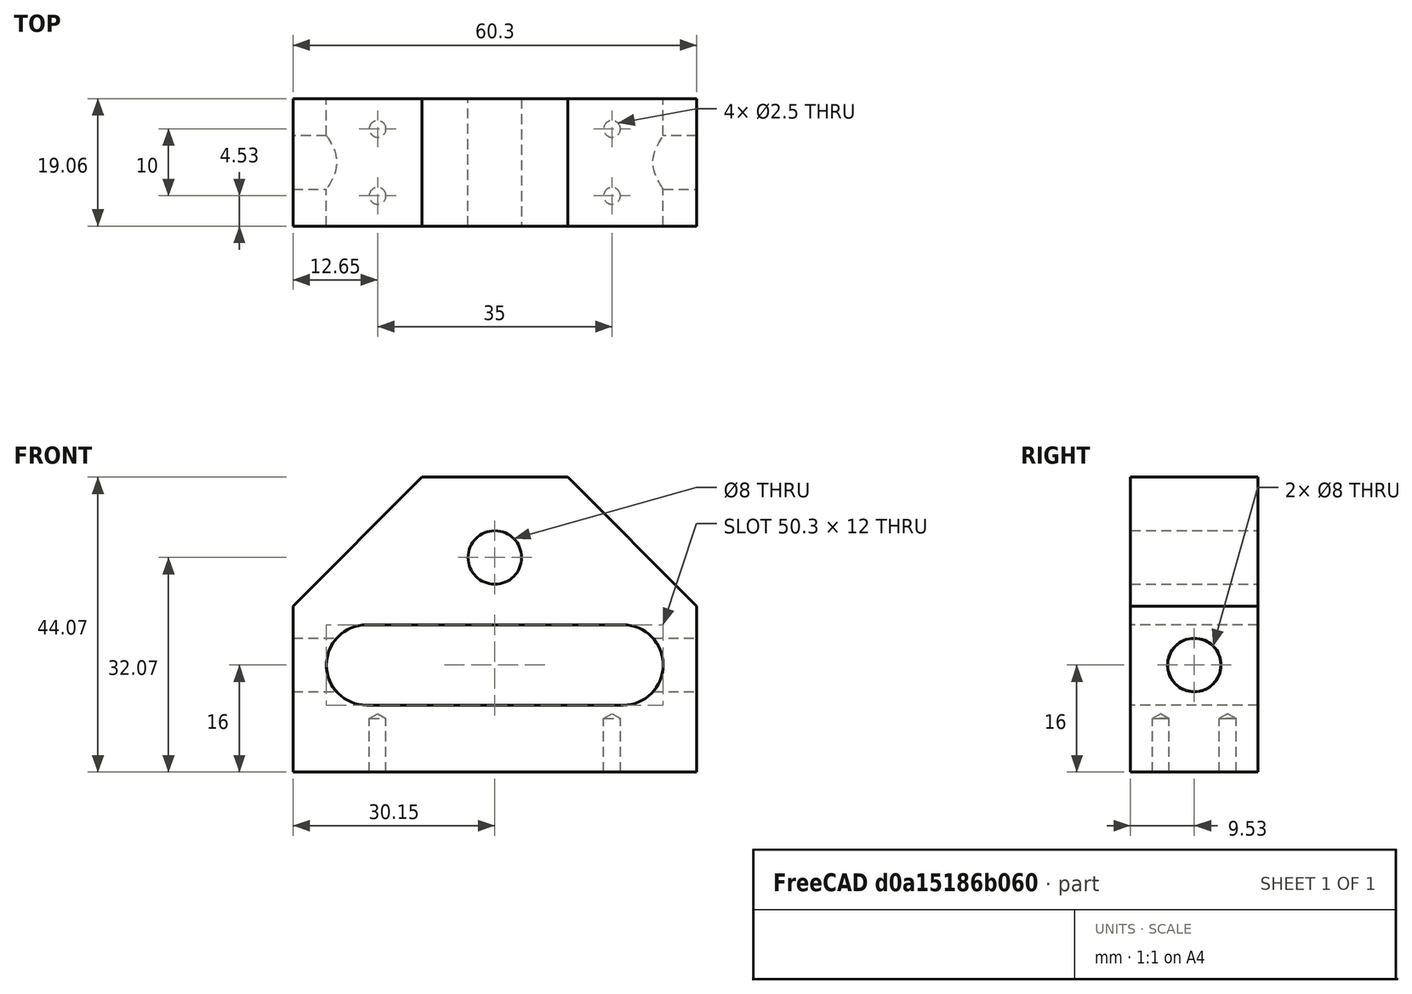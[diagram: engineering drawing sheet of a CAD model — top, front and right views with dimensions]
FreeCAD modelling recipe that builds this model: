
FCSTD DOCUMENT  (FreeCAD 0.21R33771 (Git))
Label: Alt Plate Center
License: All rights reserved
LicenseURL: http://en.wikipedia.org/wiki/All_rights_reserved
objects: TechDraw::DrawViewDimension×12, PartDesign::CoordinateSystem×5, Sketcher::SketchObject×3, TechDraw::DrawProjGroupItem×3, PartDesign::Pad×1, PartDesign::Pocket×1, TechDraw::DrawSVGTemplate×1, PartDesign::Hole×1, PartDesign::Body×1, TechDraw::DrawProjGroup×1, TechDraw::DrawViewPart×1, TechDraw::DrawPage×1
note: 32 computed .brp shape members not serialized (recipe doc carries the construction recipe); baked Part::Feature solids carry a one-line shape summary decoded from their .brp

FEATURE [Sketcher::SketchObject] Sketch
  FullyConstrained = true
  MapMode = 5
  Placement = pos=(0,0,0) rot=(1,0,0;1.5708rad)
  Support = -> [XZ_Plane002]
  sketch-geometry (14):
    g0: Circle CenterX=0 CenterY=16.0697 CenterZ=0 NormalX=0 NormalY=0 NormalZ=1 AngleXU=0 Radius=4
    g1: LineSegment StartX=-10.8804 StartY=28.0697 StartZ=0 EndX=10.8804 EndY=28.0697 EndZ=0
    g2: LineSegment StartX=0 StartY=16.0697 StartZ=0 EndX=19.1511 EndY=0 EndZ=0
    g3: LineSegment StartX=0 StartY=16.0697 StartZ=0 EndX=-19.1511 EndY=0 EndZ=0
    g4: ArcOfCircle CenterX=-19.1511 CenterY=0 CenterZ=0 NormalX=0 NormalY=0 NormalZ=1 AngleXU=0 Radius=6 StartAngle=1.5708 EndAngle=4.71239
    g5: ArcOfCircle CenterX=19.1511 CenterY=0 CenterZ=0 NormalX=0 NormalY=0 NormalZ=1 AngleXU=0 Radius=6 StartAngle=4.71239 EndAngle=7.85398
    g6: LineSegment StartX=-19.1511 StartY=-6 StartZ=0 EndX=19.1511 EndY=-6 EndZ=0
    g7: LineSegment StartX=19.1511 StartY=6 StartZ=0 EndX=-19.1511 EndY=6 EndZ=0
    g8: LineSegment StartX=-30.1511 StartY=8.79899 StartZ=0 EndX=-30.1511 EndY=-16 EndZ=0
    g9: LineSegment StartX=30.1511 StartY=-16 StartZ=0 EndX=30.1511 EndY=8.79899 EndZ=0
    g10: LineSegment StartX=30.1511 StartY=8.79899 StartZ=0 EndX=10.8804 EndY=28.0697 EndZ=0
    g11: LineSegment StartX=-10.8804 StartY=28.0697 StartZ=0 EndX=-30.1511 EndY=8.79899 EndZ=0
    g12: GeomPoint X=-25.1511 Y=0 Z=0
    g13: LineSegment StartX=-30.1511 StartY=-16 StartZ=0 EndX=30.1511 EndY=-16 EndZ=0
  constraints (35):
    c: Diameter(g0) = 8
    c: Tangent(g4,g6) = -1.5708
    c: Tangent(g6,g5) = -1.5708
    c: Tangent(g5,g7) = -1.5708
    c: Tangent(g7,g4) = -1.5708
    c: Equal(g4,g5)
    c: Coincident(g4,g3)
    c: Coincident(g5,g2)
    c: Angle(g3,g2) = 1.74533
    c: Equal(g2,g3)
    c: Distance(g2) = 25
    c: Diameter(g5) = 12
    c: Coincident(g3,g2)
    c: PointOnObject(g0,g-2)
    c: PointOnObject(g5,g-1)
    c: PointOnObject(g4,g-1)
    c: Vertical(g8)
    c: Vertical(g9)
    c: Coincident(g9,g10)
    c: Coincident(g8,g11)
    c: Coincident(g10,g1)
    c: Coincident(g1,g11)
    c: Symmetric(g1,g1,g-2)
    c: Symmetric(g8,g9,g-2)
    c: PointOnObject(g12,g4)
    c: PointOnObject(g12,g-1)
    c: Distance(g12,g8) = 5
    c: Coincident(g2,g0)
    c: Distance(g0,g1) = 12
    c: Distance(g4,g11) = 14
    c: Angle(g10,g9) = 2.35619
    c: Horizontal(g13)
    c: DistanceY(g13,g4) = 10
    c: Coincident(g13,g9)
    c: Coincident(g13,g8)
FEATURE [PartDesign::Pad] Pad
  Direction = (0,-1,-2e-16)
  Length = 19.05
  Length2 = 10
  Midplane = true
  Placement = pos=(0,0,0) rot=(1,0,0;1.5708rad)
  Profile = -> Sketch
  ReferenceAxis = -> Sketch [N_Axis]
  Type = 0
FEATURE [PartDesign::CoordinateSystem] Local_CS  label="frontLCS"
  AttacherType = Attacher::AttachEngine3D
  MapMode = 11
  Placement = pos=(0,-9.525,16.0697) rot=(0.57735,-0.57735,0.57735;2.0944rad)
FEATURE [PartDesign::CoordinateSystem] Local_CS001  label="backLCS"
  AttacherType = Attacher::AttachEngine3D
  MapMode = 11
  Placement = pos=(0,9.525,16.0697) rot=(0.57735,-0.57735,0.57735;2.0944rad)
FEATURE [PartDesign::CoordinateSystem] Local_CS002  label="baseLCS"
  AttacherType = Attacher::AttachEngine3D
  MapMode = 5
  Placement = pos=(0,-4e-15,-16) rot=(1,0,0;3.14159rad)
FEATURE [Sketcher::SketchObject] Sketch001
  FullyConstrained = true
  MapMode = 5
  Placement = pos=(0,0,0) rot=(0.57735,0.57735,0.57735;2.0944rad)
  Support = -> [YZ_Plane002]
  sketch-geometry (1):
    g0: Circle CenterX=0 CenterY=0 CenterZ=0 NormalX=0 NormalY=0 NormalZ=1 AngleXU=0 Radius=4
  constraints (2):
    c: Coincident(g0,g-1)
    c: Diameter(g0) = 8
FEATURE [PartDesign::Pocket] Pocket
  BaseFeature = -> Pad
  Direction = (-1,2e-16,-3e-16)
  Length = 5
  Length2 = 5
  Midplane = true
  Placement = pos=(0,0,0) rot=(1,0,0;1.5708rad)
  Profile = -> Sketch001
  ReferenceAxis = -> Sketch001 [N_Axis]
  Type = 1
FEATURE [PartDesign::CoordinateSystem] Local_CS003  label="threadLCS"
  AttacherType = Attacher::AttachEngine3D
  MapMode = 11
  Placement = pos=(-30.1511,7e-15,-2e-15) rot=(0.707107,0,0.707107;3.14159rad)
FEATURE [PartDesign::CoordinateSystem] Local_CS004  label="slotLCS"
  AttacherType = Attacher::AttachEngine3D
  MapMode = 45
  Placement = pos=(-0.000223577,-8.77746e-06,2.78296e-05) rot=(-1e-06,2e-06,1;1.5708rad)
FEATURE [TechDraw::DrawSVGTemplate] Template
  EditableTexts = Designed_by_Name=Rio; FC-Date=2024-05-02; FC-SH=1; FC-Title=Altitude Block
  Height = 210
  Orientation = 1
  Template = <path>
  Width = 297
FEATURE [Sketcher::SketchObject] Sketch003
  AttachmentOffset = pos=(0,0,-16) rot=(0,0,1;0rad)
  FullyConstrained = true
  MapMode = 5
  Placement = pos=(0,0,-16) rot=(0,0,1;0rad)
  Support = -> [XY_Plane002]
  sketch-geometry (9):
    g0: LineSegment StartX=-17.5 StartY=5 StartZ=0 EndX=-17.5 EndY=-5 EndZ=0
    g1: LineSegment StartX=-17.5 StartY=-5 StartZ=0 EndX=17.5 EndY=-5 EndZ=0
    g2: LineSegment StartX=17.5 StartY=-5 StartZ=0 EndX=17.5 EndY=5 EndZ=0
    g3: LineSegment StartX=17.5 StartY=5 StartZ=0 EndX=-17.5 EndY=5 EndZ=0
    g4: GeomPoint X=0 Y=0 Z=0
    g5: Circle CenterX=-17.5 CenterY=5 CenterZ=0 NormalX=0 NormalY=0 NormalZ=1 AngleXU=0 Radius=1.5
    g6: Circle CenterX=-17.5 CenterY=-5 CenterZ=0 NormalX=0 NormalY=0 NormalZ=1 AngleXU=0 Radius=1.5
    g7: Circle CenterX=17.5 CenterY=-5 CenterZ=0 NormalX=0 NormalY=0 NormalZ=1 AngleXU=0 Radius=1.5
    g8: Circle CenterX=17.5 CenterY=5 CenterZ=0 NormalX=0 NormalY=0 NormalZ=1 AngleXU=0 Radius=1.5
  constraints (20):
    c: Coincident(g0,g1)
    c: Coincident(g1,g2)
    c: Coincident(g2,g3)
    c: Coincident(g3,g0)
    c: Horizontal(g1)
    c: Horizontal(g3)
    c: Vertical(g0)
    c: Vertical(g2)
    c: Symmetric(g1,g0,g4)
    c: Coincident(g4,g-1)
    c: Coincident(g5,g0)
    c: Coincident(g6,g0)
    c: Coincident(g7,g1)
    c: Coincident(g8,g2)
    c: Equal(g8,g7)
    c: Equal(g7,g6)
    c: Equal(g6,g5)
    c: Diameter(g8) = 3
    c: DistanceX(g3,g3) = 35
    c: DistanceY(g0,g0) = 10
FEATURE [PartDesign::Hole] Hole
  BaseFeature = -> Pocket
  CustomThreadClearance = 0
  Depth = 8
  DepthType = 0
  Diameter = 2.5
  DrillForDepth = false
  DrillPoint = 1
  DrillPointAngle = 118
  HoleCutCountersinkAngle = 90
  HoleCutCustomValues = false
  HoleCutDepth = 0
  HoleCutDiameter = 6.1
  HoleCutType = 0
  ModelThread = false
  Placement = pos=(0,0,0) rot=(1,0,0;1.5708rad)
  Profile = -> Sketch003
  Reversed = true
  Tapered = false
  TaperedAngle = 90
  ThreadClass = 0
  ThreadDepth = 8
  ThreadDepthType = 0
  ThreadDirection = 0
  ThreadFit = 0
  ThreadSize = 9
  ThreadType = 1
  Threaded = true
  UseCustomThreadClearance = false
FEATURE [PartDesign::Body] Body  label="Alt Plate Center"
  Group = -> [Sketch,Pad,Local_CS,Local_CS001,Local_CS002,Sketch001,Pocket,Local_CS003,Local_CS004,Sketch003,Hole]
  Origin = -> Origin002
  Tip = -> Hole
FEATURE [TechDraw::DrawProjGroupItem] ProjItem  label="Front"
  CoarseView = false
  Direction = (0,1,0)
  Focus = 100
  HardHidden = false
  IsoCount = 0
  IsoHidden = false
  IsoVisible = false
  LockPosition = true
  Perspective = false
  Rotation = 0
  RotationVector = (-1,0,0)
  ScaleType = 2
  ScrubCount = 0
  SeamHidden = false
  SeamVisible = true
  SmoothHidden = false
  SmoothVisible = true
  Source = -> [Body]
  Type = 0
  X = 0
  XDirection = (-1,0,0)
  Y = 0
FEATURE [TechDraw::DrawProjGroupItem] ProjItem001  label="Right"
  CoarseView = false
  Direction = (-1,1e-16,0)
  Focus = 100
  HardHidden = false
  IsoCount = 0
  IsoHidden = false
  IsoVisible = false
  LockPosition = false
  Perspective = false
  Rotation = 0
  RotationVector = (1,0,0)
  ScaleType = 2
  ScrubCount = 0
  SeamHidden = false
  SeamVisible = true
  SmoothHidden = false
  SmoothVisible = true
  Source = -> [Body]
  Type = 2
  X = 86.3442
  XDirection = (-1e-16,-1,0)
  Y = 0
FEATURE [TechDraw::DrawProjGroupItem] ProjItem002  label="Bottom"
  CoarseView = false
  Direction = (0,0,-1)
  Focus = 100
  HardHidden = false
  IsoCount = 0
  IsoHidden = false
  IsoVisible = false
  LockPosition = false
  Perspective = false
  Rotation = 0
  RotationVector = (1,0,0)
  ScaleType = 2
  ScrubCount = 0
  SeamHidden = false
  SeamVisible = true
  SmoothHidden = false
  SmoothVisible = true
  Source = -> [Body]
  Type = 5
  X = 0
  XDirection = (-1,0,0)
  Y = -78.8529
FEATURE [TechDraw::DrawProjGroup] ProjGroup
  Anchor = -> ProjItem
  AutoDistribute = false
  LockPosition = false
  ProjectionType = 1
  Rotation = 0
  ScaleType = 0
  Source = -> [Body]
  Views = -> [ProjItem,ProjItem001,ProjItem002]
  X = 81.1815
  Y = 134.425
  spacingX = 15
  spacingY = 15
FEATURE [TechDraw::DrawViewPart] View
  CoarseView = false
  Direction = (-0.57735,0.57735,0.57735)
  Focus = 100
  HardHidden = false
  IsoCount = 0
  IsoHidden = false
  IsoVisible = false
  LockPosition = false
  Perspective = false
  Rotation = 0
  ScaleType = 0
  ScrubCount = 0
  SeamHidden = false
  SeamVisible = true
  SmoothHidden = false
  SmoothVisible = true
  Source = -> [Body]
  X = 237.411
  XDirection = (-0.707107,-0.707107,0)
  Y = 135.484
FEATURE [TechDraw::DrawViewDimension] Dimension
  AngleOverride = false
  Arbitrary = false
  ArbitraryTolerances = false
  EqualTolerance = true
  ExtensionAngle = 0
  FormatSpec = ⌀%.2w
  FormatSpecOverTolerance = %+.2w
  FormatSpecUnderTolerance = %+.2w
  Inverted = false
  LineAngle = 0
  LockPosition = false
  MeasureType = 1
  OverTolerance = 0
  References2D = -> [ProjItem]
  Rotation = 0
  ScaleType = 0
  TheoreticalExact = false
  Type = 5
  UnderTolerance = 0
  X = 32.8579
  Y = 33.8747
FEATURE [TechDraw::DrawViewDimension] Dimension002
  AngleOverride = false
  Arbitrary = true
  ArbitraryTolerances = false
  EqualTolerance = true
  ExtensionAngle = 0
  FormatSpec = 4x M3 ↧8
  FormatSpecOverTolerance = %+.2w
  FormatSpecUnderTolerance = %+.2w
  Inverted = false
  LineAngle = 0
  LockPosition = false
  MeasureType = 1
  OverTolerance = 0
  References2D = -> [ProjItem002]
  Rotation = 0
  ScaleType = 0
  TheoreticalExact = false
  Type = 5
  UnderTolerance = 0
  X = 2.73977
  Y = 25.5712
FEATURE [TechDraw::DrawViewDimension] Dimension007
  AngleOverride = false
  Arbitrary = false
  ArbitraryTolerances = false
  EqualTolerance = true
  ExtensionAngle = 0
  FormatSpec = %.2w
  FormatSpecOverTolerance = %+.2w
  FormatSpecUnderTolerance = %+.2w
  Inverted = false
  LineAngle = 0
  LockPosition = false
  MeasureType = 1
  OverTolerance = 0
  References2D = -> [ProjItem]
  Rotation = 0
  ScaleType = 0
  TheoreticalExact = false
  Type = 1
  UnderTolerance = 0
  X = 0.368686
  Y = 52.5009
FEATURE [TechDraw::DrawViewDimension] Dimension009
  AngleOverride = false
  Arbitrary = false
  ArbitraryTolerances = false
  EqualTolerance = true
  ExtensionAngle = 0
  FormatSpec = %.2w
  FormatSpecOverTolerance = %+.2w
  FormatSpecUnderTolerance = %+.2w
  Inverted = false
  LineAngle = 0
  LockPosition = false
  MeasureType = 1
  OverTolerance = 0
  References2D = -> [ProjItem002]
  Rotation = 0
  ScaleType = 0
  TheoreticalExact = false
  Type = 1
  UnderTolerance = 0
  X = 0
  Y = -23.9832
FEATURE [TechDraw::DrawViewDimension] Dimension010
  AngleOverride = false
  Arbitrary = false
  ArbitraryTolerances = false
  EqualTolerance = true
  ExtensionAngle = 0
  FormatSpec = %.2w
  FormatSpecOverTolerance = %+.2w
  FormatSpecUnderTolerance = %+.2w
  Inverted = false
  LineAngle = 0
  LockPosition = false
  MeasureType = 1
  OverTolerance = 0
  References2D = -> [ProjItem002]
  Rotation = 0
  ScaleType = 0
  TheoreticalExact = false
  Type = 2
  UnderTolerance = 0
  X = -44.1101
  Y = 1.87497
FEATURE [TechDraw::DrawViewDimension] Dimension012
  AngleOverride = false
  Arbitrary = false
  ArbitraryTolerances = false
  EqualTolerance = true
  ExtensionAngle = 0
  FormatSpec = ⌀%.2w
  FormatSpecOverTolerance = %+.2w
  FormatSpecUnderTolerance = %+.2w
  Inverted = false
  LineAngle = 0
  LockPosition = false
  MeasureType = 1
  OverTolerance = 0
  References2D = -> [ProjItem]
  Rotation = 0
  ScaleType = 0
  TheoreticalExact = false
  Type = 5
  UnderTolerance = 0
  X = 47.8821
  Y = 12.4022
FEATURE [TechDraw::DrawViewDimension] Dimension013
  AngleOverride = false
  Arbitrary = false
  ArbitraryTolerances = false
  EqualTolerance = true
  ExtensionAngle = 0
  FormatSpec = %.2w
  FormatSpecOverTolerance = %+.2w
  FormatSpecUnderTolerance = %+.2w
  Inverted = false
  LineAngle = 0
  LockPosition = false
  MeasureType = 1
  OverTolerance = 0
  References2D = -> [ProjItem]
  Rotation = 0
  ScaleType = 0
  TheoreticalExact = false
  Type = 2
  UnderTolerance = 0
  X = -41.1404
  Y = -6.50739
FEATURE [TechDraw::DrawViewDimension] Dimension014
  AngleOverride = false
  Arbitrary = false
  ArbitraryTolerances = false
  EqualTolerance = true
  ExtensionAngle = 0
  FormatSpec = %.2w
  FormatSpecOverTolerance = %+.2w
  FormatSpecUnderTolerance = %+.2w
  Inverted = false
  LineAngle = 0
  LockPosition = false
  MeasureType = 1
  OverTolerance = 0
  References2D = -> [ProjItem]
  Rotation = 0
  ScaleType = 0
  TheoreticalExact = false
  Type = 2
  UnderTolerance = 0
  X = -59.1354
  Y = 3.12796
FEATURE [TechDraw::DrawViewDimension] Dimension016
  AngleOverride = false
  Arbitrary = false
  ArbitraryTolerances = false
  EqualTolerance = true
  ExtensionAngle = 0
  FormatSpec = %.2w
  FormatSpecOverTolerance = %+.2w
  FormatSpecUnderTolerance = %+.2w
  Inverted = false
  LineAngle = 0
  LockPosition = false
  MeasureType = 1
  OverTolerance = 0
  References2D = -> [ProjItem]
  Rotation = 0
  ScaleType = 0
  TheoreticalExact = false
  Type = 0
  UnderTolerance = 0
  X = 53.1634
  Y = 38.5362
FEATURE [TechDraw::DrawViewDimension] Dimension017
  AngleOverride = false
  Arbitrary = false
  ArbitraryTolerances = false
  EqualTolerance = true
  ExtensionAngle = 0
  FormatSpec = %.2w
  FormatSpecOverTolerance = %+.2w
  FormatSpecUnderTolerance = %+.2w
  Inverted = false
  LineAngle = 0
  LockPosition = false
  MeasureType = 1
  OverTolerance = 0
  References2D = -> [ProjItem]
  Rotation = 0
  ScaleType = 0
  TheoreticalExact = false
  Type = 2
  UnderTolerance = 0
  X = 42.483
  Y = -9.9548
FEATURE [TechDraw::DrawViewDimension] Dimension018
  AngleOverride = false
  Arbitrary = false
  ArbitraryTolerances = false
  EqualTolerance = true
  ExtensionAngle = 0
  FormatSpec = %.2w
  FormatSpecOverTolerance = %+.2w
  FormatSpecUnderTolerance = %+.2w
  Inverted = false
  LineAngle = 0
  LockPosition = false
  MeasureType = 1
  OverTolerance = 0
  References2D = -> [ProjItem]
  Rotation = 0
  ScaleType = 0
  TheoreticalExact = false
  Type = 2
  UnderTolerance = 0
  X = 64.2826
  Y = -3.5
FEATURE [TechDraw::DrawViewDimension] Dimension019
  AngleOverride = false
  Arbitrary = false
  ArbitraryTolerances = false
  EqualTolerance = true
  ExtensionAngle = 0
  FormatSpec = ⌀%.2w
  FormatSpecOverTolerance = %+.2w
  FormatSpecUnderTolerance = %+.2w
  Inverted = false
  LineAngle = 0
  LockPosition = false
  MeasureType = 1
  OverTolerance = 0
  References2D = -> [ProjItem001]
  Rotation = 0
  ScaleType = 0
  TheoreticalExact = false
  Type = 5
  UnderTolerance = 0
  X = 25.2807
  Y = 15.8004
FEATURE [TechDraw::DrawPage] Page
  KeepUpdated = true
  NextBalloonIndex = 1
  ProjectionType = 0
  Template = -> Template
  Views = -> [ProjGroup,View,Dimension,Dimension002,Dimension007,Dimension009,Dimension010,Dimension012,Dimension013,Dimension014,Dimension016,Dimension017,Dimension018,Dimension019]
note: 1 file-system path scrubbed to <path> (originals preserved in the JSON sidecar)
